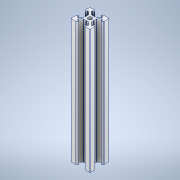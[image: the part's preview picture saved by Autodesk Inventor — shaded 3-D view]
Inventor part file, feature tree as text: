
AUTODESK INVENTOR PART (.ipt)
format: ipt  version: 2021 (Build 250183000, 183)  size: 237,568 bytes
history: native  units: mm
features: sketch x3, extrude x2, fillet x2, other x1, pattern_circular x1, hole x1, projected_geometry x1
ambient origin geometry x8: Origin, YZ Plane, XZ Plane, XY Plane, X Axis, Y Axis, Z Axis, Center Point
bodies: Body1 (feature_tree)
feature tree (11):
  other  "實體1"
  extrude  "擠出1"  Depth=20.0mm
  extrude  "擠出2"  Depth=20.0mm
  fillet  "圓角1"  Radius=130.0mm
  pattern_circular  "環形陣列1"  [2 undecoded]
  hole  "孔1"  [1 undecoded]
  fillet  "圓角2"  Radius=6.2mm
  sketch  "草圖1"
  sketch  "草圖2"
  projected_geometry  "投影迴路1"
  sketch  "草圖3"
note: 3 required parameter values undecoded (feature->parameter linkage not recoverable at this tier; creation-order binding heuristic only, values carry confidence <= 0.55)
